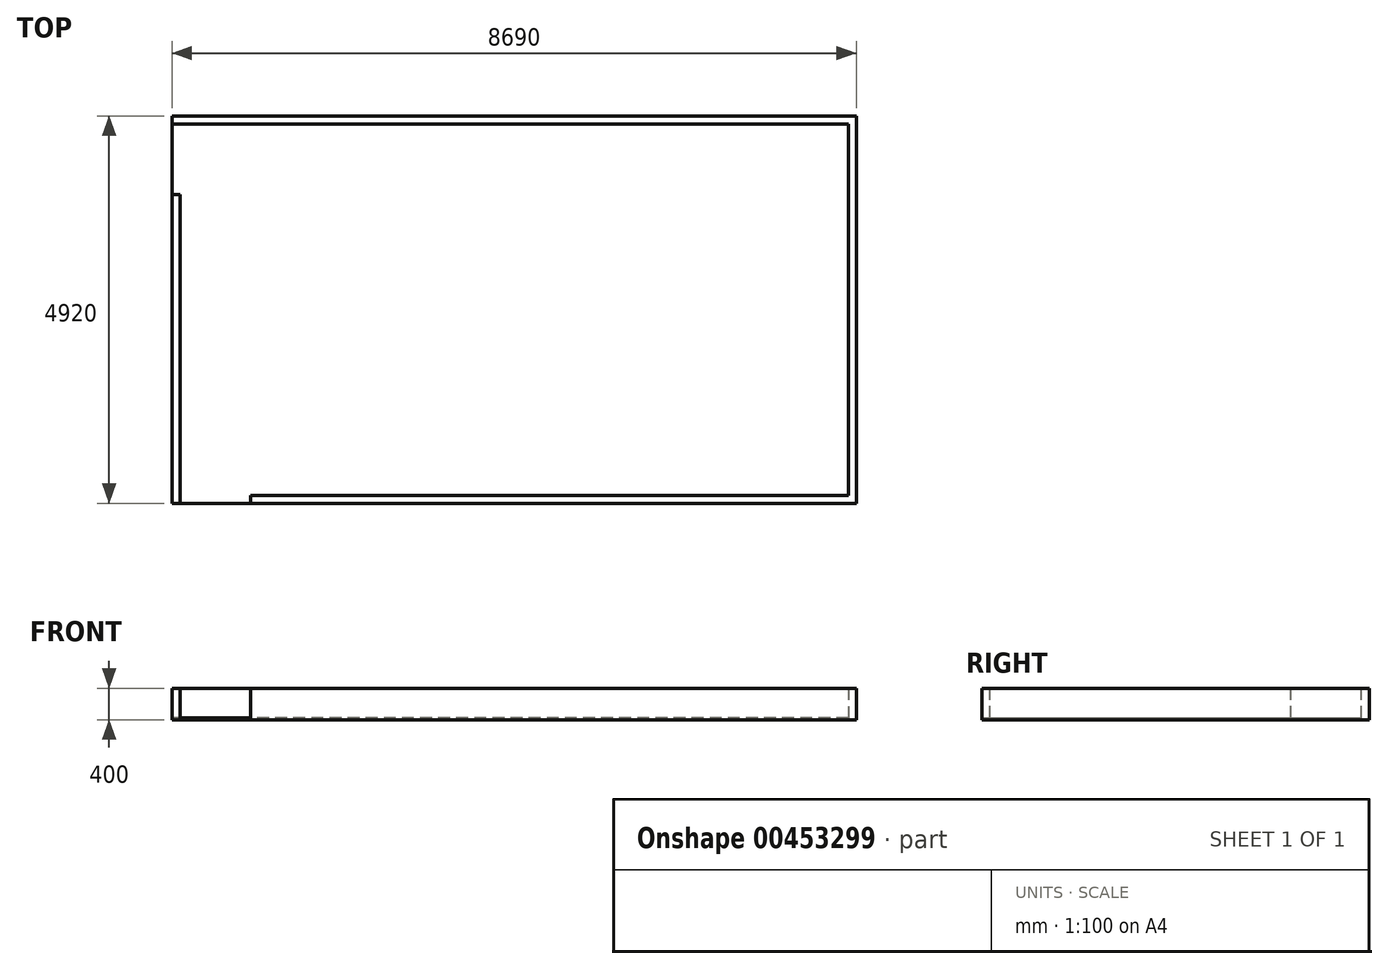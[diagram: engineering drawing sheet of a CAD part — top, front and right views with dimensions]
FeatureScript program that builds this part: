
annotation { "Feature Type Name" : "Feature", "Feature Type Description" : "" }
export const myFeature = defineFeature(function(context is Context, id is Id, definition is map)
    precondition{}
    {
        {
            var Q0;
            Q0=qCreatedBy(makeId("Top.planeOp"),FACE);
            var sketch = newSketch(context, id + "F0", { "sketchPlane" : qUnion([Q0])});
            skLineSegment(sketch, "E0.bottom", {"start": v(4245, -2360) * mm, "end": v(-4245, -2360) * mm});
            skLineSegment(sketch, "E0.top", {"start": v(4245, 2360) * mm, "end": v(-4245, 2360) * mm});
            skLineSegment(sketch, "E0.left", {"start": v(4245, -2360) * mm, "end": v(4245, 2360) * mm});
            skLineSegment(sketch, "E0.right", {"start": v(-4245, -2360) * mm, "end": v(-4245, 2360) * mm});
            skPoint(sketch, "E0.middle", {"position": v(0, 0) * mm});
            skSolve(sketch);
        }
        {
            var Q0;
            Q0 = qSketchRegion(id + "F0", true);
            extrude(context, id + "F1", {"entities" : qUnion([Q0]), "depth" : 25 * mm});
        }
        {
            var Q0;
            Q0=makeQuery(id+"F1.opExtrude","CAP_FACE",FACE,{"disambiguationData":[OSD([sQuery(id+"F0.wireOp",EDGE,"E0.bottom"),sQuery(id+"F0.wireOp",EDGE,"E0.top"),sQuery(id+"F0.wireOp",EDGE,"E0.left"),sQuery(id+"F0.wireOp",EDGE,"E0.right")])],"isStart":true});
            var sketch = newSketch(context, id + "F2", { "sketchPlane" : qUnion([Q0])});
            skLineSegment(sketch, "E1.bottom", {"start": v(4245, 2360) * mm, "end": v(-4245, 2360) * mm});
            skLineSegment(sketch, "E1.top", {"start": v(4245, -2360) * mm, "end": v(-4245, -2360) * mm});
            skLineSegment(sketch, "E1.left", {"start": v(4245, 2360) * mm, "end": v(4245, -2360) * mm});
            skLineSegment(sketch, "E1.right", {"start": v(-4245, 2360) * mm, "end": v(-4245, -2360) * mm});
            skPoint(sketch, "E1.middle", {"position": v(0, 0) * mm});
            skLineSegment(sketch, "E2.bottom", {"start": v(4345, -2460) * mm, "end": v(-4345, -2460) * mm});
            skLineSegment(sketch, "E2.top", {"start": v(4345, 2460) * mm, "end": v(-4345, 2460) * mm});
            skLineSegment(sketch, "E2.left", {"start": v(4345, -2460) * mm, "end": v(4345, 2460) * mm});
            skLineSegment(sketch, "E2.right", {"start": v(-4345, -2460) * mm, "end": v(-4345, 2460) * mm});
            skSolve(sketch);
        }
        {
            var Q0;
            Q0 = qSketchRegion(id + "F2", true);
            extrude(context, id + "F3", {"entities" : qUnion([Q0]), "operationType" : NewBodyOperationType.ADD, "oppositeDirection" : true, "depth" : 400 * mm});
        }
        {
            var Q0;
            Q0=makeQuery(id+"F3.opExtrude","CAP_FACE",FACE,{"disambiguationData":[OSD([sQuery(id+"F2.wireOp",EDGE,"E1.bottom"),sQuery(id+"F2.wireOp",EDGE,"E1.top"),sQuery(id+"F2.wireOp",EDGE,"E1.left"),sQuery(id+"F2.wireOp",EDGE,"E1.right"),sQuery(id+"F2.wireOp",EDGE,"E2.bottom"),sQuery(id+"F2.wireOp",EDGE,"E2.top"),sQuery(id+"F2.wireOp",EDGE,"E2.left"),sQuery(id+"F2.wireOp",EDGE,"E2.right")])],"isStart":false});
            var sketch = newSketch(context, id + "F4", { "sketchPlane" : qUnion([Q0])});
            skLineSegment(sketch, "E3.bottom", {"start": v(-4245, 2360) * mm, "end": v(-4345, 2360) * mm});
            skLineSegment(sketch, "E3.top", {"start": v(-4245, 1460) * mm, "end": v(-4345, 1460) * mm});
            skLineSegment(sketch, "E3.left", {"start": v(-4245, 2360) * mm, "end": v(-4245, 1460) * mm});
            skLineSegment(sketch, "E3.right", {"start": v(-4345, 2360) * mm, "end": v(-4345, 1460) * mm});
            skLineSegment(sketch, "E4.bottom", {"start": v(-4245, -2360) * mm, "end": v(-3345, -2360) * mm});
            skLineSegment(sketch, "E4.top", {"start": v(-4245, -2460) * mm, "end": v(-3345, -2460) * mm});
            skLineSegment(sketch, "E4.left", {"start": v(-4245, -2360) * mm, "end": v(-4245, -2460) * mm});
            skLineSegment(sketch, "E4.right", {"start": v(-3345, -2360) * mm, "end": v(-3345, -2460) * mm});
            skSolve(sketch);
        }
        {
            var Q0;
            Q0 = qSketchRegion(id + "F4", true);
            var Q1;
            Q1=makeQuery(id+"F1.opExtrude","CAP_FACE",FACE,{"disambiguationData":[OSD([sQuery(id+"F0.wireOp",EDGE,"E0.bottom"),sQuery(id+"F0.wireOp",EDGE,"E0.top"),sQuery(id+"F0.wireOp",EDGE,"E0.left"),sQuery(id+"F0.wireOp",EDGE,"E0.right")])],"isStart":false});
            extrude(context, id + "F5", {"entities" : qUnion([Q0]), "operationType" : NewBodyOperationType.REMOVE, "endBound" : BoundingType.UP_TO_SURFACE, "oppositeDirection" : true, "endBoundEntityFace" : qUnion([Q1]), "depth" : 25 * mm});
        }
    });
